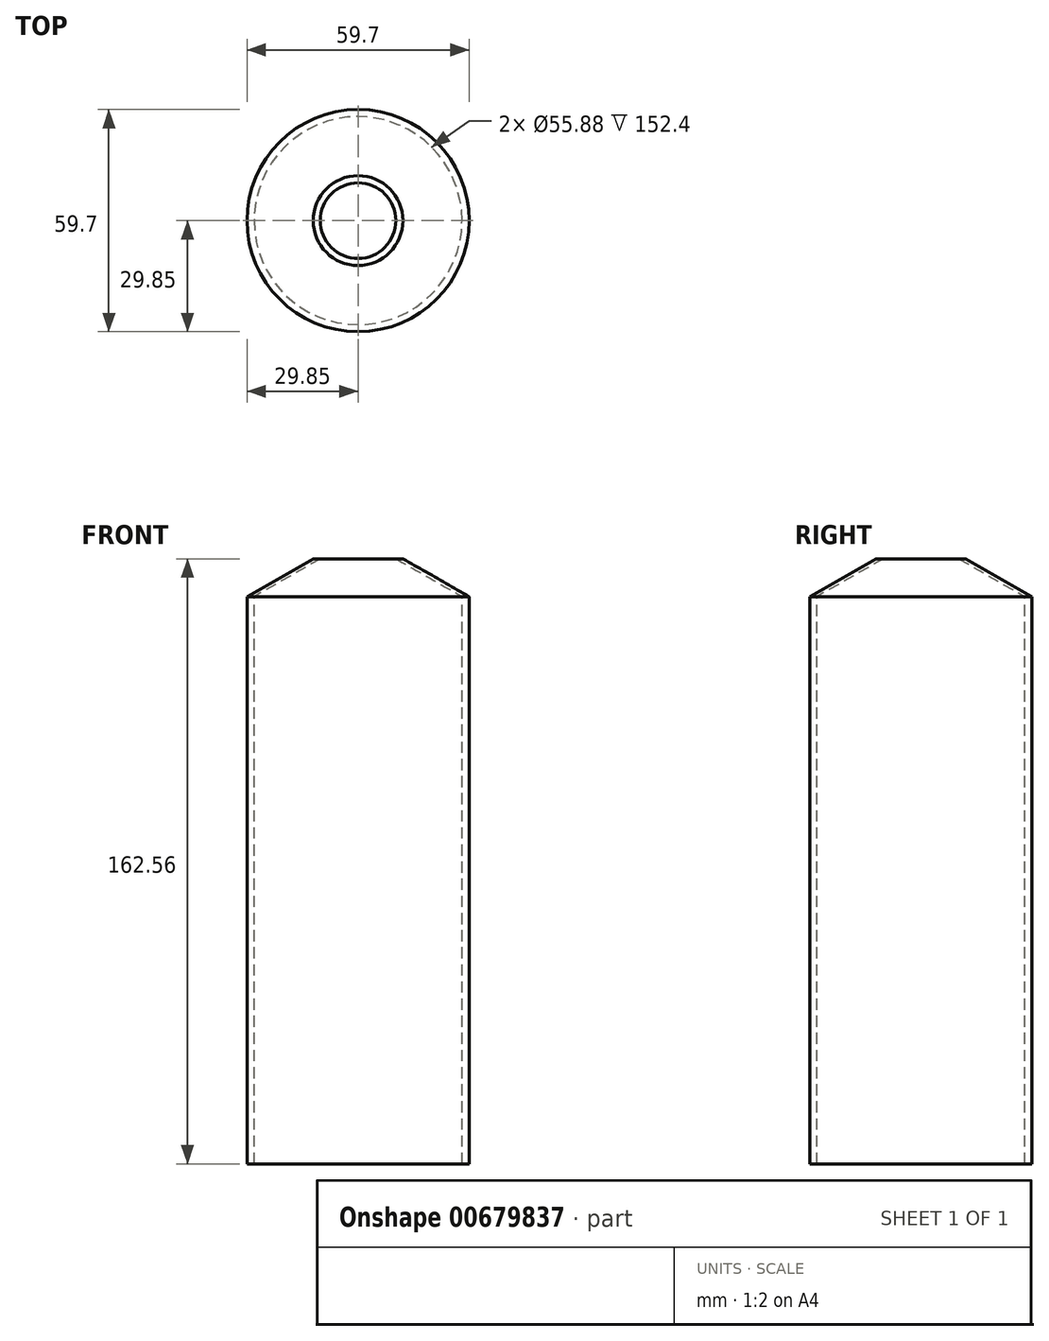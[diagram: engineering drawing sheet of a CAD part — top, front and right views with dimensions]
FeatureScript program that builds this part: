
annotation { "Feature Type Name" : "Feature", "Feature Type Description" : "" }
export const myFeature = defineFeature(function(context is Context, id is Id, definition is map)
    precondition{}
    {
        {
            var Q0;
            Q0=qCreatedBy(makeId("Front.planeOp"),FACE);
            var sketch = newSketch(context, id + "F0", { "sketchPlane" : qUnion([Q0])});
            skLineSegment(sketch, "E0", {"start": v(0, 76.28) * mm, "end": v(0, -76.12) * mm});
            skLineSegment(sketch, "E1", {"start": v(-27.94, 76.28) * mm, "end": v(-27.94, -76.12) * mm});
            skLineSegment(sketch, "E2", {"start": v(27.94, 76.28) * mm, "end": v(27.94, -76.12) * mm});
            skLineSegment(sketch, "E3", {"start": v(-27.94, -76.12) * mm, "end": v(-29.84, -76.12) * mm});
            skLineSegment(sketch, "E4", {"start": v(27.94, -76.12) * mm, "end": v(29.85, -76.12) * mm});
            skLineSegment(sketch, "E5", {"start": v(29.85, -76.12) * mm, "end": v(29.85, 76.28) * mm});
            skLineSegment(sketch, "E6", {"start": v(-29.85, 76.28) * mm, "end": v(-29.84, -76.12) * mm});
            skLineSegment(sketch, "E7", {"start": v(0, 76.28) * mm, "end": v(0, 86.44) * mm});
            skLineSegment(sketch, "E8", {"start": v(10.16, 86.44) * mm, "end": v(27.94, 76.28) * mm});
            skLineSegment(sketch, "E9", {"start": v(-10.16, 86.44) * mm, "end": v(-27.94, 76.28) * mm});
            skLineSegment(sketch, "E10", {"start": v(-10.16, 86.44) * mm, "end": v(-12.07, 86.44) * mm});
            skLineSegment(sketch, "E11", {"start": v(-12.07, 86.44) * mm, "end": v(-29.85, 76.28) * mm});
            skLineSegment(sketch, "E12", {"start": v(10.16, 86.44) * mm, "end": v(12.07, 86.44) * mm});
            skLineSegment(sketch, "E13", {"start": v(12.07, 86.44) * mm, "end": v(29.85, 76.28) * mm});
            skLineSegment(sketch, "E14", {"start": v(0, 86.44) * mm, "end": v(0, -76.12) * mm, "construction": true});
            skLineSegment(sketch, "E15", {"start": v(0, 0) * mm, "end": v(0, 76.28) * mm, "construction": true});
            skSolve(sketch);
        }
        {
            var Q0;
            Q0 = qSketchRegion(id + "F0", true);
            var Q1;
            Q1=sQuery(id+"F0.wireOp",EDGE,"E0");
            revolve(context, id + "F1", {"entities" : qUnion([Q0]), "axis" : qUnion([Q1]), "revolveType" : RevolveType.FULL});
        }
    });
